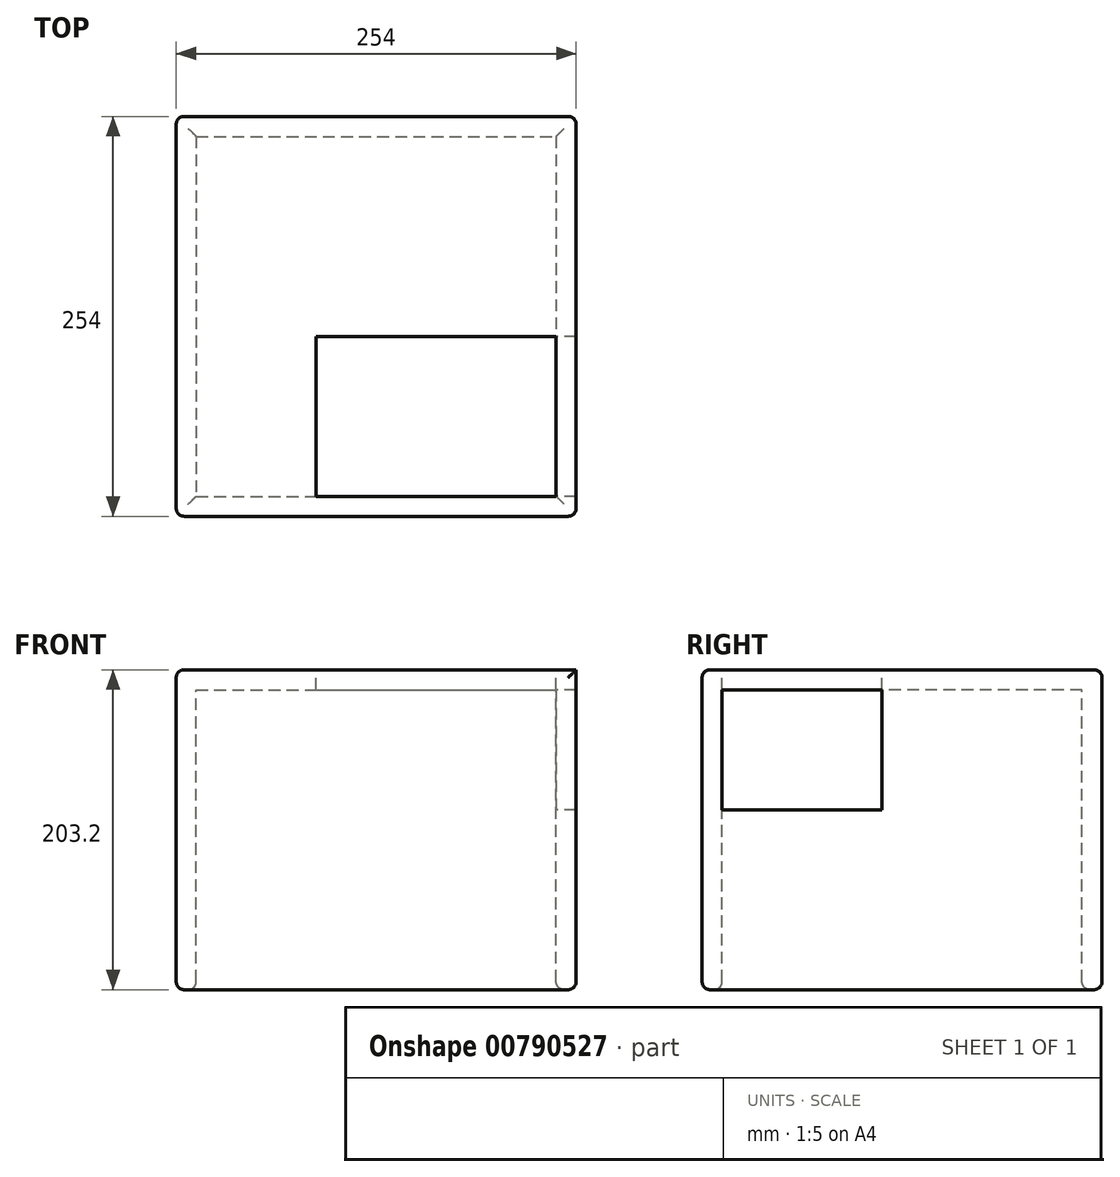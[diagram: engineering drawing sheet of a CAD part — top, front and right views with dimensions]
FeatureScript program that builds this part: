
annotation { "Feature Type Name" : "Feature", "Feature Type Description" : "" }
export const myFeature = defineFeature(function(context is Context, id is Id, definition is map)
    precondition{}
    {
        {
            var Q0;
            Q0=qCreatedBy(makeId("Top.planeOp"),FACE);
            var sketch = newSketch(context, id + "F0", { "sketchPlane" : qUnion([Q0])});
            skLineSegment(sketch, "E0.bottom", {"start": v(-201.77, 205.6) * mm, "end": v(52.23, 205.6) * mm});
            skLineSegment(sketch, "E0.top", {"start": v(-201.77, -48.4) * mm, "end": v(52.23, -48.4) * mm});
            skLineSegment(sketch, "E0.left", {"start": v(-201.77, 205.6) * mm, "end": v(-201.77, -48.4) * mm});
            skLineSegment(sketch, "E0.right", {"start": v(52.23, 205.6) * mm, "end": v(52.23, -48.4) * mm});
            skLineSegment(sketch, "E1.bottom", {"start": v(-189.07, 192.9) * mm, "end": v(39.53, 192.9) * mm});
            skLineSegment(sketch, "E1.top", {"start": v(-189.07, -35.7) * mm, "end": v(39.53, -35.7) * mm});
            skLineSegment(sketch, "E1.left", {"start": v(-189.07, 192.9) * mm, "end": v(-189.07, -35.7) * mm});
            skLineSegment(sketch, "E1.right", {"start": v(39.53, 192.9) * mm, "end": v(39.53, -35.7) * mm});
            skSolve(sketch);
        }
        {
            var Q0;
            Q0=makeQuery(id+"F0.imprint","IMPRINT",FACE,{"disambiguationData":[TD([[makeQuery(id+"F0.imprint","IMPRINT",EDGE,{"derivedFrom":sQuery(id+"F0.wireOp",EDGE,"E0.bottom")}),-1.0]])]});
            var Q1;
            Q1=makeQuery(id+"F0.imprint","IMPRINT",FACE,{"disambiguationData":[TD([[makeQuery(id+"F0.imprint","IMPRINT",EDGE,{"derivedFrom":sQuery(id+"F0.wireOp",EDGE,"E1.bottom")}),-1.0]])]});
            var Q2;
            Q2=sQuery(id+"F0.wireOp",EDGE,"E1.top");
            var Q3;
            Q3=sQuery(id+"F0.wireOp",EDGE,"E1.bottom");
            var Q4;
            Q4=sQuery(id+"F0.wireOp",EDGE,"E0.right");
            var Q5;
            Q5=sQuery(id+"F0.wireOp",EDGE,"E0.left");
            var Q6;
            Q6=sQuery(id+"F0.wireOp",EDGE,"E0.top");
            var Q7;
            Q7=sQuery(id+"F0.wireOp",EDGE,"E0.bottom");
            var Q8;
            Q8=sQuery(id+"F0.wireOp",EDGE,"E1.left");
            var Q9;
            Q9=sQuery(id+"F0.wireOp",EDGE,"E1.right");
            extrude(context, id + "F1", {"entities" : qUnion([Q0, Q1]), "surfaceEntities" : qUnion([Q2, Q3, Q4, Q5, Q6, Q7, Q8, Q9]), "oppositeDirection" : true, "depth" : 203.2 * mm, "offsetDistance" : 25.4 * mm});
        }
        {
            var Q0;
            Q0=makeQuery(id+"F1.opExtrude","CAP_FACE",FACE,{"disambiguationData":[OSD([sQuery(id+"F0.wireOp",EDGE,"E0.bottom"),sQuery(id+"F0.wireOp",EDGE,"E0.top"),sQuery(id+"F0.wireOp",EDGE,"E0.left"),sQuery(id+"F0.wireOp",EDGE,"E0.right")])],"isStart":false});
            shell(context, id + "F2", {"entities" : qUnion([Q0]), "thickness" : 12.7 * mm});
        }
        {
            var Q0;
            Q0=qCreatedBy(makeId("Top.planeOp"),FACE);
            var sketch = newSketch(context, id + "F3", { "sketchPlane" : qUnion([Q0])});
            skLineSegment(sketch, "E2.bottom", {"start": v(-112.87, 65.9) * mm, "end": v(39.53, 65.9) * mm});
            skLineSegment(sketch, "E2.top", {"start": v(-112.87, -35.7) * mm, "end": v(39.53, -35.7) * mm});
            skLineSegment(sketch, "E2.left", {"start": v(-112.87, 65.9) * mm, "end": v(-112.87, -35.7) * mm});
            skLineSegment(sketch, "E2.right", {"start": v(39.53, 65.9) * mm, "end": v(39.53, -35.7) * mm});
            skSolve(sketch);
        }
        {
            var Q0;
            Q0 = qSketchRegion(id + "F3", true);
            extrude(context, id + "F4", {"entities" : qUnion([Q0]), "operationType" : NewBodyOperationType.REMOVE, "oppositeDirection" : true, "depth" : 12.7 * mm, "offsetDistance" : 25.4 * mm});
        }
        {
            var Q0;
            Q0=qCreatedBy(makeId("Right.planeOp"),FACE);
            var sketch = newSketch(context, id + "F5", { "sketchPlane" : qUnion([Q0])});
            skLineSegment(sketch, "E3.bottom", {"start": v(-35.7, -12.7) * mm, "end": v(65.9, -12.7) * mm});
            skLineSegment(sketch, "E3.top", {"start": v(-35.7, -88.9) * mm, "end": v(65.9, -88.9) * mm});
            skLineSegment(sketch, "E3.left", {"start": v(-35.7, -12.7) * mm, "end": v(-35.7, -88.9) * mm});
            skLineSegment(sketch, "E3.right", {"start": v(65.9, -12.7) * mm, "end": v(65.9, -88.9) * mm});
            skSolve(sketch);
        }
        {
            var Q0;
            Q0 = qSketchRegion(id + "F5", true);
            extrude(context, id + "F6", {"entities" : qUnion([Q0]), "operationType" : NewBodyOperationType.REMOVE, "depth" : 76.2 * mm, "offsetDistance" : 25.4 * mm});
        }
        {
            var Q0;
            Q0=makeQuery(id+"F1.opExtrude","SWEPT_FACE",FACE,{"disambiguationData":[OSD([sQuery(id+"F0.wireOp",EDGE,"E0.bottom")])]});
            fillet(context, id + "F7", {"entities" : qUnion([Q0]), "radius" : 5.08 * mm, "tangentPropagation" : true, "allowEdgeOverflow" : false});
        }
        {
            var Q0;
            Q0=makeQuery(id+"F1.opExtrude","SWEPT_FACE",FACE,{"disambiguationData":[OSD([sQuery(id+"F0.wireOp",EDGE,"E0.top")])]});
            fillet(context, id + "F8", {"entities" : qUnion([Q0]), "radius" : 5.08 * mm, "tangentPropagation" : true, "allowEdgeOverflow" : false});
        }
        {
            var Q0;
            Q0=makeQuery(id+"F1.opExtrude","SWEPT_FACE",FACE,{"disambiguationData":[OSD([sQuery(id+"F0.wireOp",EDGE,"E0.left")])]});
            fillet(context, id + "F9", {"entities" : qUnion([Q0]), "radius" : 5.08 * mm, "tangentPropagation" : true, "allowEdgeOverflow" : false});
        }
        {
            var Q0;
            Q0=makeQuery(id+"F1.opExtrude","CAP_FACE",FACE,{"disambiguationData":[OSD([sQuery(id+"F0.wireOp",EDGE,"E0.bottom"),sQuery(id+"F0.wireOp",EDGE,"E0.top"),sQuery(id+"F0.wireOp",EDGE,"E0.left"),sQuery(id+"F0.wireOp",EDGE,"E0.right")])],"isStart":false});
            fillet(context, id + "F10", {"entities" : qUnion([Q0]), "radius" : 5.08 * mm, "tangentPropagation" : true, "allowEdgeOverflow" : false});
        }
    });
